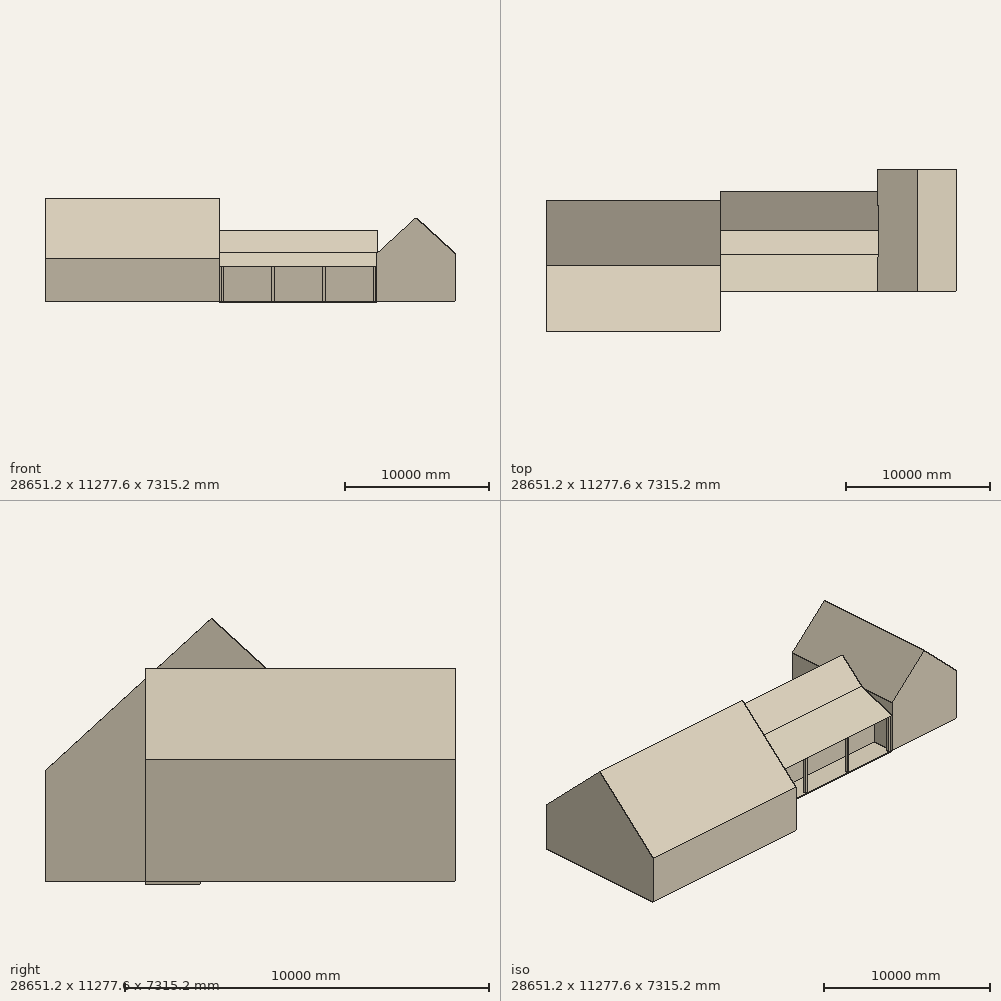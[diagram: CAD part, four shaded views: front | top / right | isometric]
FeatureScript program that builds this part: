
annotation { "Feature Type Name" : "Feature", "Feature Type Description" : "" }
export const myFeature = defineFeature(function(context is Context, id is Id, definition is map)
    precondition{}
    {
        {
            var Q0;
            Q0=qCreatedBy(makeId("Top.planeOp"),FACE);
            var sketch = newSketch(context, id + "F0", { "sketchPlane" : qUnion([Q0])});
            skLineSegment(sketch, "E0.bottom", {"start": v(0, 0) * mm, "end": v(10972.8, 0) * mm});
            skLineSegment(sketch, "E0.top", {"start": v(0, 5486.4) * mm, "end": v(10972.8, 5486.4) * mm});
            skLineSegment(sketch, "E0.left", {"start": v(0, 0) * mm, "end": v(0, 5486.4) * mm});
            skLineSegment(sketch, "E0.right", {"start": v(10972.8, 0) * mm, "end": v(10972.8, 5486.4) * mm});
            skLineSegment(sketch, "E1", {"start": v(0, 4876.8) * mm, "end": v(-12192, 4876.8) * mm});
            skLineSegment(sketch, "E2", {"start": v(-12192, 4876.8) * mm, "end": v(-12192, -4267.2) * mm});
            skLineSegment(sketch, "E3", {"start": v(-12192, -4267.2) * mm, "end": v(0, -4267.2) * mm});
            skLineSegment(sketch, "E4", {"start": v(0, -4267.2) * mm, "end": v(0, 0) * mm});
            skLineSegment(sketch, "E5", {"start": v(10972.8, 0) * mm, "end": v(10972.8, -1524) * mm});
            skLineSegment(sketch, "E6", {"start": v(10972.8, -1524) * mm, "end": v(16459.2, -1524) * mm});
            skLineSegment(sketch, "E7", {"start": v(16459.2, -1524) * mm, "end": v(16459.2, 7010.4) * mm});
            skLineSegment(sketch, "E8", {"start": v(16459.2, 7010.4) * mm, "end": v(10972.8, 7010.4) * mm});
            skLineSegment(sketch, "E9", {"start": v(10972.8, 7010.4) * mm, "end": v(10972.8, 5486.4) * mm});
            skLineSegment(sketch, "E10", {"start": v(10972.8, -1524) * mm, "end": v(0, -1524) * mm});
            skLineSegment(sketch, "E11.bottom", {"start": v(76.2, -1295.4) * mm, "end": v(228.6, -1295.4) * mm});
            skLineSegment(sketch, "E11.left", {"start": v(76.2, -1295.4) * mm, "end": v(76.2, -1447.8) * mm});
            skLineSegment(sketch, "E11.right", {"start": v(228.6, -1295.4) * mm, "end": v(228.6, -1447.8) * mm});
            skLineSegment(sketch, "E12.bottom", {"start": v(10896.6, -1447.8) * mm, "end": v(10744.2, -1447.8) * mm});
            skLineSegment(sketch, "E12.top", {"start": v(10896.6, -1295.4) * mm, "end": v(10744.2, -1295.4) * mm});
            skLineSegment(sketch, "E12.left", {"start": v(10896.6, -1447.8) * mm, "end": v(10896.6, -1295.4) * mm});
            skLineSegment(sketch, "E12.right", {"start": v(10744.2, -1447.8) * mm, "end": v(10744.2, -1295.4) * mm});
            skLineSegment(sketch, "E13.bottom", {"start": v(7188.2, -1447.8) * mm, "end": v(7340.6, -1447.8) * mm});
            skLineSegment(sketch, "E13.top", {"start": v(7188.2, -1295.4) * mm, "end": v(7340.6, -1295.4) * mm});
            skLineSegment(sketch, "E13.left", {"start": v(7188.2, -1447.8) * mm, "end": v(7188.2, -1295.4) * mm});
            skLineSegment(sketch, "E13.right", {"start": v(7340.6, -1447.8) * mm, "end": v(7340.6, -1295.4) * mm});
            skLineSegment(sketch, "E14.bottom", {"start": v(3632.2, -1447.8) * mm, "end": v(3784.6, -1447.8) * mm});
            skLineSegment(sketch, "E14.top", {"start": v(3632.2, -1295.4) * mm, "end": v(3784.6, -1295.4) * mm});
            skLineSegment(sketch, "E14.left", {"start": v(3632.2, -1447.8) * mm, "end": v(3632.2, -1295.4) * mm});
            skLineSegment(sketch, "E14.right", {"start": v(3784.6, -1447.8) * mm, "end": v(3784.6, -1295.4) * mm});
            skLineSegment(sketch, "E15", {"start": v(228.6, -1447.8) * mm, "end": v(3632.2, -1447.8) * mm});
            skLineSegment(sketch, "E16", {"start": v(3784.6, -1447.8) * mm, "end": v(7188.2, -1447.8) * mm});
            skLineSegment(sketch, "E17", {"start": v(7340.6, -1447.8) * mm, "end": v(10744.2, -1447.8) * mm});
            skLineSegment(sketch, "E18", {"start": v(228.6, -1447.8) * mm, "end": v(76.2, -1447.8) * mm});
            skSolve(sketch);
        }
        {
            var Q0;
            {var subQ0=sQuery(id+"F0.wireOp",EDGE,"E1");Q0=makeQuery(id+"F0.imprint","IMPRINT",FACE,{"disambiguationData":[TD([[makeQuery(id+"F0.imprint","IMPRINT",EDGE,{"derivedFrom":subQ0}),1.0]])]});}
            extrude(context, id + "F1", {"entities" : qUnion([Q0]), "depth" : 3048 * mm, "offsetDistance" : 30.48 * mm});
        }
        {
            var Q0;
            Q0=makeQuery(id+"F1.opExtrude","SWEPT_FACE",FACE,{"disambiguationData":[OSD([sQuery(id+"F0.wireOp",EDGE,"E2")])]});
            var sketch = newSketch(context, id + "F2", { "sketchPlane" : qUnion([Q0])});
            skLineSegment(sketch, "E19", {"start": v(-304.8, 7239) * mm, "end": v(-4876.8, 3048) * mm});
            skLineSegment(sketch, "E20", {"start": v(-304.8, 7239) * mm, "end": v(4267.2, 3048) * mm});
            skSolve(sketch);
        }
        {
            var Q0;
            Q0=makeQuery(id+"F2.imprint","IMPRINT",FACE,{"disambiguationData":[TD([[makeQuery(id+"F2.imprint","IMPRINT",EDGE,{"derivedFrom":sQuery(id+"F2.wireOp",EDGE,"E19")}),1.0]])]});
            var Q1;
            Q1=makeQuery(id+"F1.opExtrude","SWEPT_FACE",FACE,{"disambiguationData":[OSD([sQuery(id+"F0.wireOp",EDGE,"E0.left"),sQuery(id+"F0.wireOp",EDGE,"E4")])]});
            extrude(context, id + "F3", {"entities" : qUnion([Q0]), "operationType" : NewBodyOperationType.ADD, "endBound" : BoundingType.UP_TO_SURFACE, "oppositeDirection" : true, "depth" : 30.48 * mm, "endBoundEntityFace" : qUnion([Q1]), "offsetDistance" : 30.48 * mm});
        }
        {
            var Q0;
            {var subQ3=sQuery(id+"F0.wireOp",EDGE,"E0.bottom");Q0=makeQuery(id+"F0.imprint","IMPRINT",FACE,{"disambiguationData":[TD([[makeQuery(id+"F0.imprint","IMPRINT",EDGE,{"derivedFrom":subQ3}),1.0]])]});}
            extrude(context, id + "F4", {"entities" : qUnion([Q0]), "operationType" : NewBodyOperationType.ADD, "depth" : 2438.4 * mm, "offsetDistance" : 30.48 * mm});
        }
        {
            var Q0;
            Q0=makeQuery(id+"F4.opExtrude","SWEPT_FACE",FACE,{"disambiguationData":[OSD([sQuery(id+"F0.wireOp",EDGE,"E0.right")])]});
            var sketch = newSketch(context, id + "F5", { "sketchPlane" : qUnion([Q0])});
            skLineSegment(sketch, "E21", {"start": v(1081.57, 3429.84) * mm, "end": v(2743.2, 4953) * mm});
            skLineSegment(sketch, "E22", {"start": v(2743.2, 4953) * mm, "end": v(5486.4, 2438.4) * mm});
            skLineSegment(sketch, "E23", {"start": v(0, 2438.4) * mm, "end": v(-1524, 2438.4) * mm});
            skLineSegment(sketch, "E24", {"start": v(-1524, 2438.4) * mm, "end": v(1081.57, 3429.84) * mm});
            skSolve(sketch);
        }
        {
            var Q0;
            Q0=makeQuery(id+"F5.imprint","IMPRINT",FACE,{"disambiguationData":[TD([[makeQuery(id+"F5.imprint","IMPRINT",EDGE,{"derivedFrom":sQuery(id+"F5.wireOp",EDGE,"E21")}),-1.0]])]});
            var Q1;
            Q1=makeQuery(id+"F3.boolean.opBoolean","MERGE",FACE,{"derivedFrom":[makeQuery(id+"F1.opExtrude","SWEPT_FACE",FACE,{"disambiguationData":[OSD([sQuery(id+"F0.wireOp",EDGE,"E0.left"),sQuery(id+"F0.wireOp",EDGE,"E4")])]}),makeQuery(id+"F3.opExtrude","CAP_FACE",FACE,{"disambiguationData":[OSD([sQuery(id+"F0.wireOp",EDGE,"E2"),sQuery(id+"F2.wireOp",EDGE,"E19"),sQuery(id+"F2.wireOp",EDGE,"E20")])],"isStart":false})]});
            extrude(context, id + "F6", {"entities" : qUnion([Q0]), "operationType" : NewBodyOperationType.ADD, "endBound" : BoundingType.UP_TO_SURFACE, "oppositeDirection" : true, "depth" : 30.48 * mm, "endBoundEntityFace" : qUnion([Q1]), "offsetDistance" : 30.48 * mm});
        }
        {
            var Q0;
            Q0=makeQuery(id+"F0.imprint","IMPRINT",FACE,{"disambiguationData":[TD([[makeQuery(id+"F0.imprint","IMPRINT",EDGE,{"derivedFrom":sQuery(id+"F0.wireOp",EDGE,"E0.right")}),-1.0]])]});
            extrude(context, id + "F7", {"entities" : qUnion([Q0]), "operationType" : NewBodyOperationType.ADD, "depth" : 3352.8 * mm, "offsetDistance" : 30.48 * mm});
        }
        {
            var Q0;
            {var subQ0=sQuery(id+"F0.wireOp",EDGE,"E0.bottom");Q0=makeQuery(id+"F0.imprint","IMPRINT",FACE,{"disambiguationData":[TD([[makeQuery(id+"F0.imprint","IMPRINT",EDGE,{"derivedFrom":subQ0}),-1.0]])]});}
            extrude(context, id + "F8", {"entities" : qUnion([Q0]), "oppositeDirection" : true, "depth" : 76.2 * mm, "offsetDistance" : 30.48 * mm});
        }
        {
            var Q0;
            Q0=makeQuery(id+"F0.imprint","IMPRINT",FACE,{"disambiguationData":[TD([[makeQuery(id+"F0.imprint","IMPRINT",EDGE,{"derivedFrom":sQuery(id+"F0.wireOp",EDGE,"E11.bottom")}),-1.0]])]});
            var Q1;
            Q1=makeQuery(id+"F6.opExtrude","SWEPT_FACE",FACE,{"disambiguationData":[OSD([sQuery(id+"F0.wireOp",EDGE,"E0.right"),sQuery(id+"F5.wireOp",EDGE,"E23")])]});
            extrude(context, id + "F9", {"entities" : qUnion([Q0]), "operationType" : NewBodyOperationType.ADD, "endBound" : BoundingType.UP_TO_SURFACE, "depth" : 30.48 * mm, "endBoundEntityFace" : qUnion([Q1]), "offsetDistance" : 30.48 * mm});
        }
        {
            var Q0;
            Q0=makeQuery(id+"F7.opExtrude","SWEPT_FACE",FACE,{"disambiguationData":[OSD([sQuery(id+"F0.wireOp",EDGE,"E6")])]});
            var sketch = newSketch(context, id + "F10", { "sketchPlane" : qUnion([Q0])});
            skLineSegment(sketch, "E25", {"start": v(10972.8, 3352.8) * mm, "end": v(13716, 5867.4) * mm});
            skLineSegment(sketch, "E26", {"start": v(13716, 5867.4) * mm, "end": v(16459.2, 3352.8) * mm});
            skSolve(sketch);
        }
        {
            var Q0;
            Q0=makeQuery(id+"F10.imprint","IMPRINT",FACE,{"disambiguationData":[TD([[makeQuery(id+"F10.imprint","IMPRINT",EDGE,{"derivedFrom":sQuery(id+"F10.wireOp",EDGE,"E25")}),-1.0]])]});
            var Q1;
            Q1=makeQuery(id+"F7.opExtrude","SWEPT_FACE",FACE,{"disambiguationData":[OSD([sQuery(id+"F0.wireOp",EDGE,"E8")])]});
            extrude(context, id + "F11", {"entities" : qUnion([Q0]), "operationType" : NewBodyOperationType.ADD, "endBound" : BoundingType.UP_TO_SURFACE, "oppositeDirection" : true, "depth" : 30.48 * mm, "endBoundEntityFace" : qUnion([Q1]), "offsetDistance" : 30.48 * mm});
        }
        {
            var Q0;
            Q0=makeQuery(id+"F0.imprint","IMPRINT",FACE,{"disambiguationData":[TD([[makeQuery(id+"F0.imprint","IMPRINT",EDGE,{"derivedFrom":sQuery(id+"F0.wireOp",EDGE,"E12.bottom")}),-1.0]])]});
            var Q1;
            Q1=makeQuery(id+"F6.opExtrude","SWEPT_FACE",FACE,{"disambiguationData":[OSD([sQuery(id+"F0.wireOp",EDGE,"E0.right"),sQuery(id+"F5.wireOp",EDGE,"E23")])]});
            extrude(context, id + "F12", {"entities" : qUnion([Q0]), "operationType" : NewBodyOperationType.ADD, "endBound" : BoundingType.UP_TO_SURFACE, "depth" : 30.48 * mm, "endBoundEntityFace" : qUnion([Q1]), "offsetDistance" : 30.48 * mm});
        }
        {
            var Q0;
            Q0=makeQuery(id+"F0.imprint","IMPRINT",FACE,{"disambiguationData":[TD([[makeQuery(id+"F0.imprint","IMPRINT",EDGE,{"derivedFrom":sQuery(id+"F0.wireOp",EDGE,"E13.bottom")}),1.0]])]});
            var Q1;
            Q1=makeQuery(id+"F6.opExtrude","SWEPT_FACE",FACE,{"disambiguationData":[OSD([sQuery(id+"F0.wireOp",EDGE,"E0.right"),sQuery(id+"F5.wireOp",EDGE,"E23")])]});
            extrude(context, id + "F13", {"entities" : qUnion([Q0]), "operationType" : NewBodyOperationType.ADD, "endBound" : BoundingType.UP_TO_SURFACE, "depth" : 30.48 * mm, "endBoundEntityFace" : qUnion([Q1]), "offsetDistance" : 30.48 * mm});
        }
        {
            var Q0;
            Q0=makeQuery(id+"F0.imprint","IMPRINT",FACE,{"disambiguationData":[TD([[makeQuery(id+"F0.imprint","IMPRINT",EDGE,{"derivedFrom":sQuery(id+"F0.wireOp",EDGE,"E14.bottom")}),1.0]])]});
            var Q1;
            Q1=makeQuery(id+"F6.opExtrude","SWEPT_FACE",FACE,{"disambiguationData":[OSD([sQuery(id+"F0.wireOp",EDGE,"E0.right"),sQuery(id+"F5.wireOp",EDGE,"E23")])]});
            extrude(context, id + "F14", {"entities" : qUnion([Q0]), "operationType" : NewBodyOperationType.ADD, "endBound" : BoundingType.UP_TO_SURFACE, "depth" : 30.48 * mm, "endBoundEntityFace" : qUnion([Q1]), "offsetDistance" : 30.48 * mm});
        }
    });
